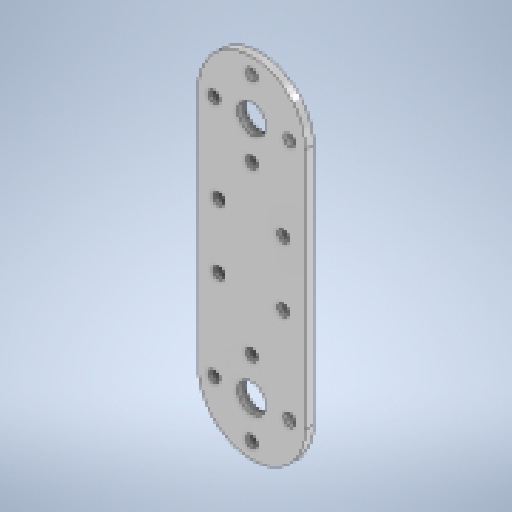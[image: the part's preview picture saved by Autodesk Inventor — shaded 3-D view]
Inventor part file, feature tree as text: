
AUTODESK INVENTOR PART (.ipt)
format: ipt  version: 2024.1 (Build 281209000, 209)  size: 192,000 bytes
history: native  units: in
note: dims shown in document units (in); Inventor stores cm internally (conversion verified against a paired STEP export)
features: reference x9, sketch x4, other x4, hole x2, sheet_metal_op x1, extrude x1
ambient origin geometry x8: Origin, YZ Plane, XZ Plane, XY Plane, X Axis, Y Axis, Z Axis, Center Point
bodies: Solid1 (feature_tree)
feature tree (21):
  sheet_metal_op  "Face1"
  hole  "Hole1"  [1 undecoded]
  extrude  "Extrusion1"  TaperAngle=0.0deg  [1 undecoded]
  hole  "Hole2"  [1 undecoded]
  sketch  "Sketch1"  dims[d0=0.7843in d1=1.7717in]
  other  "Plate1"
  sketch  "Sketch2"  dims[d2=0.0591in]
  reference  "Reference1"
  reference  "Reference2"
  reference  "Reference3"
  reference  "Reference4"
  sketch  "Sketch3"  dims[d3=0.0827in d4=0.1181in d5=0.119in d6=0.0787in d7=0.5635in d8=0.0591in d9=0.0in]
  reference  "Reference5"
  sketch  "Sketch4"  dims[d10=0.2047in d11=0.0in d12=0.0in d13=0.0827in d14=2.1331in d15=0.119in d16=0.0787in d17=0.5635in d18=0.0591in d19=0.8108in]
  reference  "Reference6"
  reference  "Reference7"
  reference  "Reference8"
  reference  "Reference9"
  other  "2_Arm.iam"
  other  "Top Horn:2"
  other  "axis_3_bottom_frame(middle):1"
note: 3 required parameter values undecoded (feature->parameter linkage not recoverable at this tier; creation-order binding heuristic only, values carry confidence <= 0.55)
